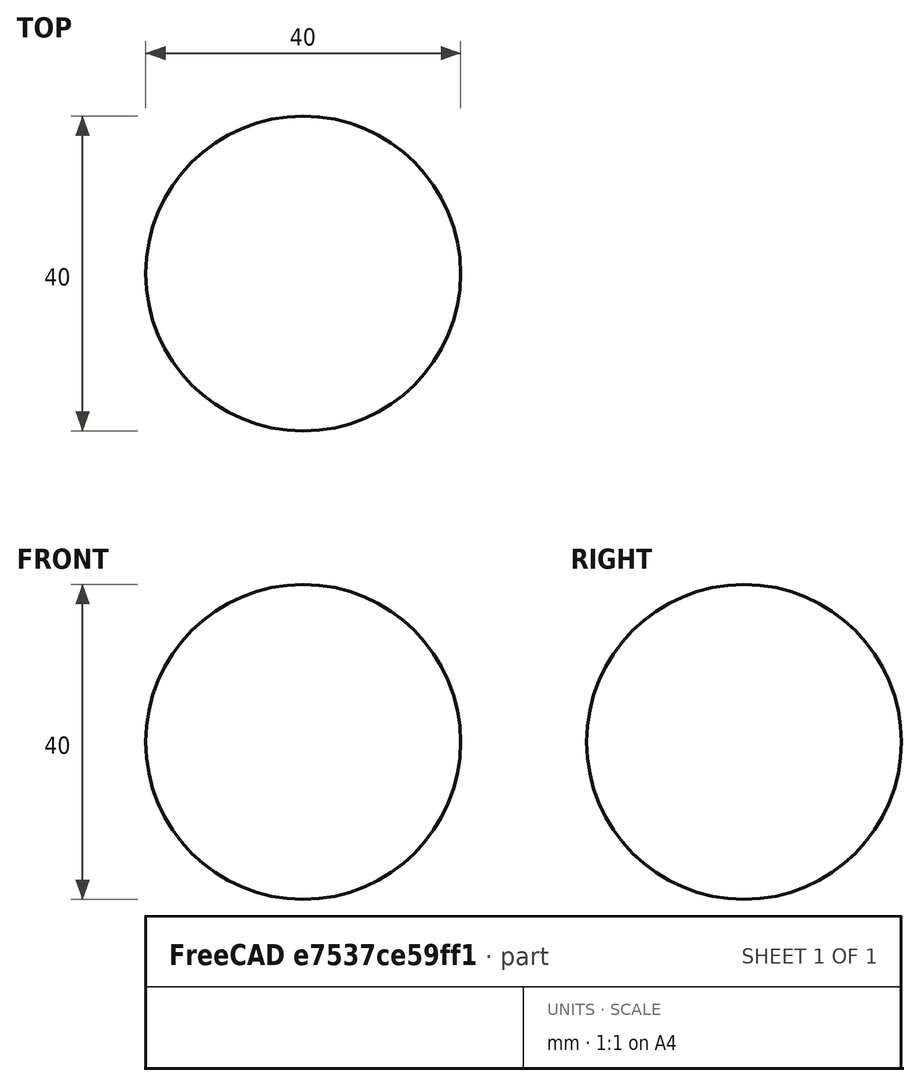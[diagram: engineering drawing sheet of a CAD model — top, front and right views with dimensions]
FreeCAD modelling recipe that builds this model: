
FCSTD DOCUMENT  (FreeCAD 0.21R33668 +7 (Git))
Label: ball
License: All rights reserved
LicenseURL: https://en.wikipedia.org/wiki/All_rights_reserved
objects: Sketcher::SketchObject×1, PartDesign::Revolution×1, PartDesign::Body×1
note: 4 computed .brp shape members not serialized (recipe doc carries the construction recipe); baked Part::Feature solids carry a one-line shape summary decoded from their .brp

FEATURE [Sketcher::SketchObject] Sketch
  FullyConstrained = true
  MapMode = 5
  Placement = pos=(0,0,0) rot=(1,0,0;1.5708rad)
  Support = -> [XZ_Plane]
  sketch-geometry (2):
    g0: ArcOfCircle CenterX=0 CenterY=0 CenterZ=0 NormalX=0 NormalY=0 NormalZ=1 AngleXU=0 Radius=20 StartAngle=1.5708 EndAngle=4.71239
    g1: LineSegment StartX=0 StartY=20 StartZ=0 EndX=0 EndY=-20 EndZ=0
  constraints (6):
    c: Coincident(g0,g-1)
    c: Coincident(g1,g0)
    c: Coincident(g1,g0)
    c: Vertical(g1)
    c: PointOnObject(g0,g1)
    c: DistanceY(g1,g1) = 40
FEATURE [PartDesign::Revolution] Revolution
  Angle = 360
  Axis = (0,2e-16,1)
  Base = (0,0,0)
  Placement = pos=(0,0,0) rot=(1,0,0;1.5708rad)
  Profile = -> Sketch
  ReferenceAxis = -> Sketch [V_Axis]
FEATURE [PartDesign::Body] Body  label="ball"
  Group = -> [Sketch,Revolution]
  Origin = -> Origin
  Tip = -> Revolution
